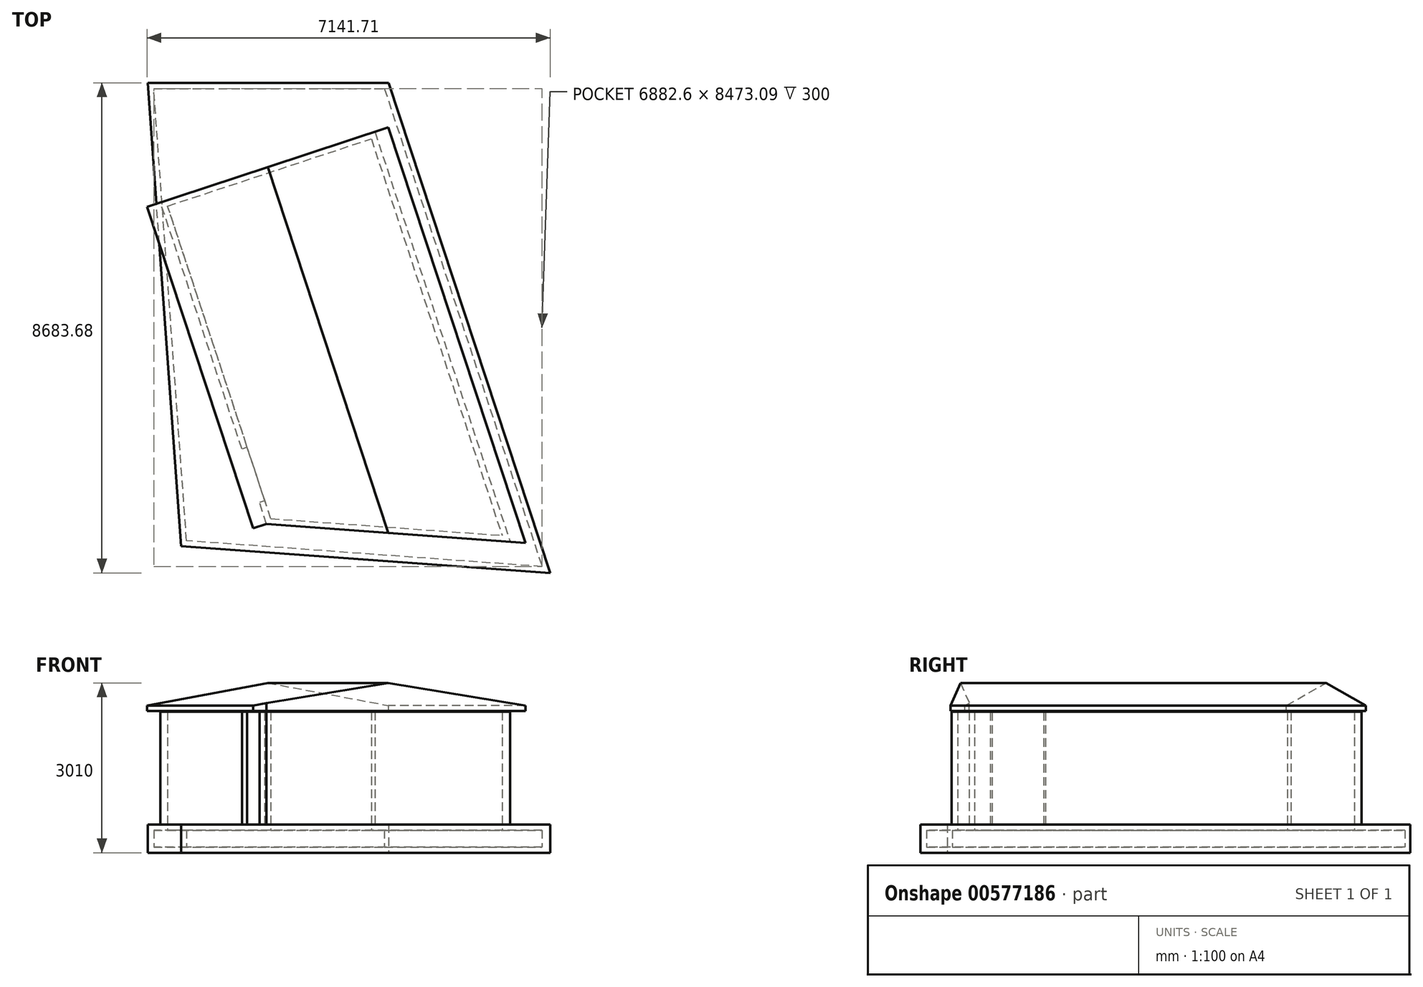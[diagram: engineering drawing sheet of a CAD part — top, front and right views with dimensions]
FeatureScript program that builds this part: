
annotation { "Feature Type Name" : "Feature", "Feature Type Description" : "" }
export const myFeature = defineFeature(function(context is Context, id is Id, definition is map)
    precondition{}
    {
        {
            var Q0;
            Q0=qCreatedBy(makeId("Top.planeOp"),FACE);
            var sketch = newSketch(context, id + "F0", { "sketchPlane" : qUnion([Q0])});
            skLineSegment(sketch, "E0", {"start": v(-2799.1, 3209.55) * mm, "end": v(1468.1, 3209.55) * mm});
            skLineSegment(sketch, "E1", {"start": v(1468.1, 3209.55) * mm, "end": v(4332.8, -5474.13) * mm});
            skLineSegment(sketch, "E2", {"start": v(4332.8, -5474.13) * mm, "end": v(-2203.11, -4998.44) * mm});
            skLineSegment(sketch, "E3", {"start": v(-2203.11, -4998.44) * mm, "end": v(-2799.1, 3209.55) * mm});
            skSolve(sketch);
        }
        {
            var Q0;
            Q0=makeQuery(id+"F0.imprint","IMPRINT",FACE,{"disambiguationData":[TD([[makeQuery(id+"F0.imprint","IMPRINT",EDGE,{"derivedFrom":sQuery(id+"F0.wireOp",EDGE,"E0")}),-1.0]])]});
            extrude(context, id + "F1", {"entities" : qUnion([Q0]), "depth" : 500 * mm, "offsetDistance" : 25 * mm});
        }
        {
            var Q0;
            Q0=makeQuery(id+"F1.opExtrude","CAP_FACE",FACE,{"disambiguationData":[OSD([sQuery(id+"F0.wireOp",EDGE,"E0"),sQuery(id+"F0.wireOp",EDGE,"E1"),sQuery(id+"F0.wireOp",EDGE,"E2"),sQuery(id+"F0.wireOp",EDGE,"E3")])],"isStart":false});
            var sketch = newSketch(context, id + "F2", { "sketchPlane" : qUnion([Q0])});
            skLineSegment(sketch, "E4", {"start": v(1227.13, 2343.99) * mm, "end": v(3106.86, -3353.96) * mm});
            skLineSegment(sketch, "E5", {"start": v(3106.86, -3353.96) * mm, "end": v(-691.77, -4607.12) * mm});
            skLineSegment(sketch, "E6", {"start": v(-691.77, -4607.12) * mm, "end": v(-2571.5, 1090.83) * mm});
            skLineSegment(sketch, "E7", {"start": v(-2571.5, 1090.83) * mm, "end": v(1227.13, 2343.99) * mm});
            skLineSegment(sketch, "E8", {"start": v(-691.77, -4607.12) * mm, "end": v(3623.89, -4921.2) * mm});
            skLineSegment(sketch, "E9", {"start": v(3623.89, -4921.2) * mm, "end": v(3106.86, -3353.96) * mm});
            skSolve(sketch);
        }
        {
            var Q0;
            Q0=makeQuery(id+"F2.imprint","IMPRINT",FACE,{"disambiguationData":[TD([[makeQuery(id+"F2.imprint","IMPRINT",EDGE,{"derivedFrom":sQuery(id+"F2.wireOp",EDGE,"E4")}),-1.0]])]});
            extrude(context, id + "F3", {"entities" : qUnion([Q0]), "operationType" : NewBodyOperationType.ADD, "depth" : 2000 * mm, "offsetDistance" : 25 * mm});
        }
        {
            var Q0;
            Q0=makeQuery(id+"F3.opExtrude","SWEPT_FACE",FACE,{"disambiguationData":[OSD([sQuery(id+"F2.wireOp",EDGE,"E7")])]});
            var sketch = newSketch(context, id + "F4", { "sketchPlane" : qUnion([Q0])});
            skLineSegment(sketch, "E10", {"start": v(-2149.7, 2510) * mm, "end": v(2350.3, 2510) * mm});
            skLineSegment(sketch, "E11", {"start": v(2350.3, 2510) * mm, "end": v(2350.3, 2610) * mm});
            skLineSegment(sketch, "E12", {"start": v(2350.3, 2610) * mm, "end": v(100.3, 3010) * mm});
            skLineSegment(sketch, "E13", {"start": v(100.3, 3010) * mm, "end": v(-2149.7, 2610) * mm});
            skLineSegment(sketch, "E14", {"start": v(-2149.7, 2610) * mm, "end": v(-2149.7, 2510) * mm});
            skSolve(sketch);
        }
        {
            var Q0;
            Q0=makeQuery(id+"F4.imprint","IMPRINT",FACE,{"disambiguationData":[TD([[makeQuery(id+"F4.imprint","IMPRINT",EDGE,{"derivedFrom":sQuery(id+"F4.wireOp",EDGE,"E10")}),1.0]])]});
            var Q1;
            Q1=makeQuery(id+"F3.opExtrude","SWEPT_FACE",FACE,{"disambiguationData":[OSD([sQuery(id+"F2.wireOp",EDGE,"E5")])]});
            extrude(context, id + "F5", {"entities" : qUnion([Q0]), "endBound" : BoundingType.UP_TO_SURFACE, "oppositeDirection" : true, "depth" : 25 * mm, "endBoundEntityFace" : qUnion([Q1]), "offsetDistance" : 25 * mm});
        }
        {
            var Q0;
            Q0=makeQuery(id+"F2.imprint","IMPRINT",FACE,{"disambiguationData":[TD([[makeQuery(id+"F2.imprint","IMPRINT",EDGE,{"derivedFrom":sQuery(id+"F2.wireOp",EDGE,"E5")}),1.0]])]});
            extrude(context, id + "F6", {"entities" : qUnion([Q0]), "operationType" : NewBodyOperationType.ADD, "depth" : 2000 * mm, "offsetDistance" : 25 * mm});
        }
        {
            var Q0;
            Q0=makeQuery(id+"F5.opExtrude","CAP_FACE",FACE,{"disambiguationData":[OSD([sQuery(id+"F4.wireOp",EDGE,"E10"),sQuery(id+"F4.wireOp",EDGE,"E11"),sQuery(id+"F4.wireOp",EDGE,"E12"),sQuery(id+"F4.wireOp",EDGE,"E13"),sQuery(id+"F4.wireOp",EDGE,"E14")])],"isStart":false});
            var Q1;
            Q1=makeQuery(id+"F6.opExtrude","SWEPT_FACE",FACE,{"disambiguationData":[OSD([sQuery(id+"F2.wireOp",EDGE,"E8")])]});
            extrude(context, id + "F7", {"entities" : qUnion([Q0]), "operationType" : NewBodyOperationType.ADD, "endBound" : BoundingType.UP_TO_SURFACE, "depth" : 25 * mm, "endBoundEntityFace" : qUnion([Q1]), "offsetDistance" : 25 * mm});
        }
        {
            var Q0;
            {var subQ0=sQuery(id+"F2.wireOp",EDGE,"E5");Q0=makeQuery(id+"F6.boolean.opBoolean","MERGE",FACE,{"derivedFrom":[makeQuery(id+"F3.opExtrude","CAP_FACE",FACE,{"disambiguationData":[OSD([sQuery(id+"F2.wireOp",EDGE,"E4"),subQ0,sQuery(id+"F2.wireOp",EDGE,"E6"),sQuery(id+"F2.wireOp",EDGE,"E7")])],"isStart":false}),makeQuery(id+"F6.opExtrude","CAP_FACE",FACE,{"disambiguationData":[OSD([subQ0,sQuery(id+"F2.wireOp",EDGE,"E8"),sQuery(id+"F2.wireOp",EDGE,"E9")])],"isStart":false})]});}
            shell(context, id + "F8", {"entities" : qUnion([Q0]), "thickness" : 100 * mm});
        }
        {
            var Q0;
            Q0=makeQuery(id+"F3.opExtrude","SWEPT_FACE",FACE,{"disambiguationData":[OSD([sQuery(id+"F2.wireOp",EDGE,"E6")])]});
            var sketch = newSketch(context, id + "F9", { "sketchPlane" : qUnion([Q0])});
            skLineSegment(sketch, "E15.bottom", {"start": v(2760.25, 500) * mm, "end": v(3760.25, 500) * mm});
            skLineSegment(sketch, "E15.top", {"start": v(2760.25, 2500) * mm, "end": v(3760.25, 2500) * mm});
            skLineSegment(sketch, "E15.left", {"start": v(2760.25, 500) * mm, "end": v(2760.25, 2500) * mm});
            skLineSegment(sketch, "E15.right", {"start": v(3760.25, 500) * mm, "end": v(3760.25, 2500) * mm});
            skSolve(sketch);
        }
        {
            var Q0;
            Q0=makeQuery(id+"F9.imprint","IMPRINT",FACE,{"disambiguationData":[TD([[makeQuery(id+"F9.imprint","IMPRINT",EDGE,{"derivedFrom":sQuery(id+"F9.wireOp",EDGE,"E15.bottom")}),-1.0]])]});
            extrude(context, id + "F10", {"entities" : qUnion([Q0]), "operationType" : NewBodyOperationType.REMOVE, "oppositeDirection" : true, "depth" : 100 * mm, "offsetDistance" : 25 * mm});
        }
    });
